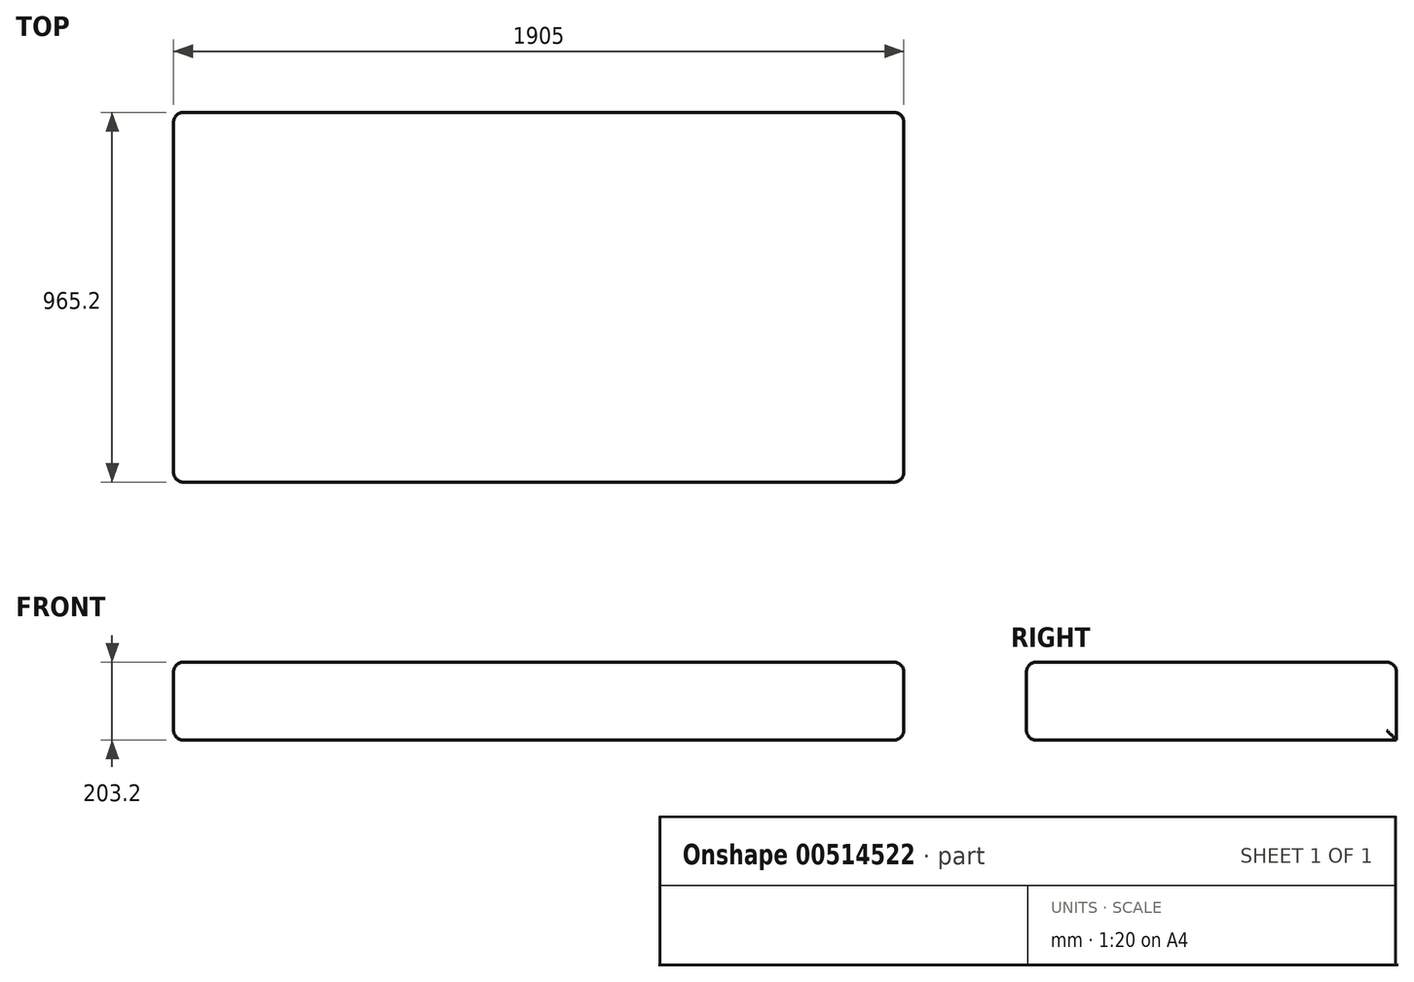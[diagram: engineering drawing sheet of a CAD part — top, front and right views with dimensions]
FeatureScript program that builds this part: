
annotation { "Feature Type Name" : "Feature", "Feature Type Description" : "" }
export const myFeature = defineFeature(function(context is Context, id is Id, definition is map)
    precondition{}
    {
        {
            var Q0;
            Q0=qCreatedBy(makeId("Top.planeOp"),FACE);
            var sketch = newSketch(context, id + "F0", { "sketchPlane" : qUnion([Q0])});
            skLineSegment(sketch, "E0.bottom", {"start": v(0, 0) * mm, "end": v(1905, 0) * mm});
            skLineSegment(sketch, "E0.top", {"start": v(0, -965.2) * mm, "end": v(1905, -965.2) * mm});
            skLineSegment(sketch, "E0.left", {"start": v(0, 0) * mm, "end": v(0, -965.2) * mm});
            skLineSegment(sketch, "E0.right", {"start": v(1905, 0) * mm, "end": v(1905, -965.2) * mm});
            skSolve(sketch);
        }
        {
            var Q0;
            Q0=makeQuery(id+"F0.imprint","IMPRINT",FACE,{"disambiguationData":[TD([[makeQuery(id+"F0.imprint","IMPRINT",EDGE,{"derivedFrom":sQuery(id+"F0.wireOp",EDGE,"E0.bottom")}),-1.0]])]});
            extrude(context, id + "F1", {"entities" : qUnion([Q0]), "depth" : 203.2 * mm, "offsetDistance" : 25.4 * mm});
        }
        {
            var Q0;
            Q0=makeQuery(id+"F1.opExtrude","CAP_FACE",FACE,{"disambiguationData":[OSD([sQuery(id+"F0.wireOp",EDGE,"E0.bottom"),sQuery(id+"F0.wireOp",EDGE,"E0.top"),sQuery(id+"F0.wireOp",EDGE,"E0.left"),sQuery(id+"F0.wireOp",EDGE,"E0.right")])],"isStart":false});
            var Q1;
            Q1=makeQuery(id+"F1.opExtrude","SWEPT_FACE",FACE,{"disambiguationData":[OSD([sQuery(id+"F0.wireOp",EDGE,"E0.right")])]});
            var Q2;
            Q2=makeQuery(id+"F1.opExtrude","CAP_EDGE",EDGE,{"disambiguationData":[OSD([sQuery(id+"F0.wireOp",EDGE,"E0.top")])],"isStart":true});
            var Q3;
            Q3=makeQuery(id+"F1.opExtrude","SWEPT_FACE",FACE,{"disambiguationData":[OSD([sQuery(id+"F0.wireOp",EDGE,"E0.left")])]});
            fillet(context, id + "F2", {"entities" : qUnion([Q0, Q1, Q2, Q3]), "radius" : 25.4 * mm, "tangentPropagation" : true, "allowEdgeOverflow" : false});
        }
    });
